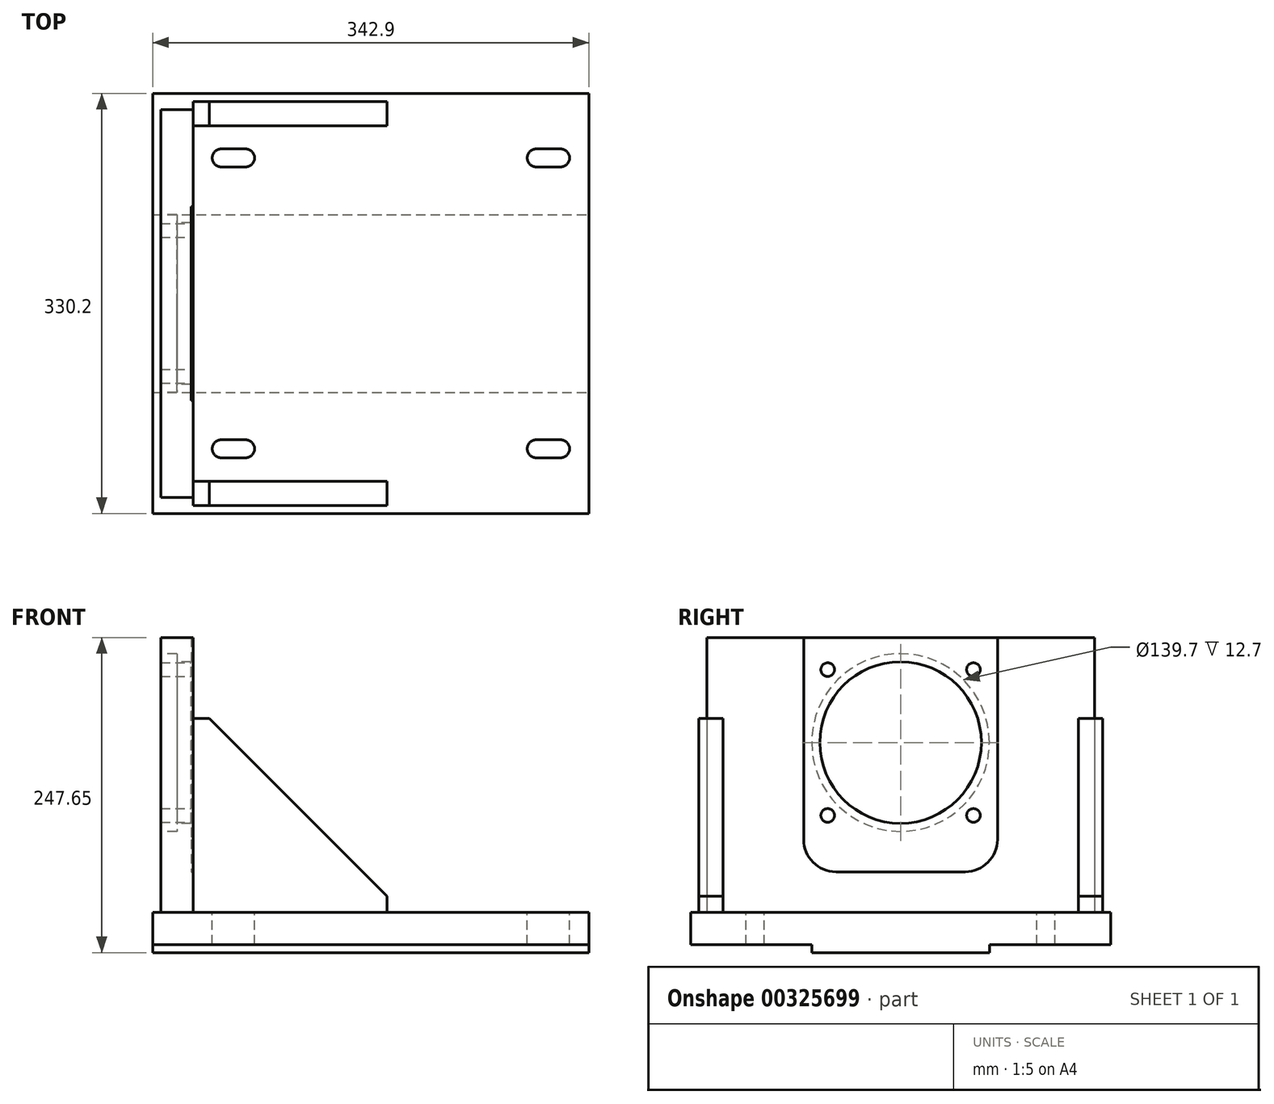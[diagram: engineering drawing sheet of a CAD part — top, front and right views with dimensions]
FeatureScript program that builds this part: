
annotation { "Feature Type Name" : "Feature", "Feature Type Description" : "" }
export const myFeature = defineFeature(function(context is Context, id is Id, definition is map)
    precondition{}
    {
        {
            var Q0;
            Q0=qCreatedBy(makeId("Top.planeOp"),FACE);
            var sketch = newSketch(context, id + "F0", { "sketchPlane" : qUnion([Q0])});
            skLineSegment(sketch, "E0.bottom", {"start": v(-171.45, 165.1) * mm, "end": v(171.45, 165.1) * mm});
            skLineSegment(sketch, "E0.top", {"start": v(-171.45, -165.1) * mm, "end": v(171.45, -165.1) * mm});
            skLineSegment(sketch, "E0.left", {"start": v(-171.45, 165.1) * mm, "end": v(-171.45, -165.1) * mm});
            skLineSegment(sketch, "E0.right", {"start": v(171.45, 165.1) * mm, "end": v(171.45, -165.1) * mm});
            skPoint(sketch, "E0.middle", {"position": v(0, 0) * mm});
            skLineSegment(sketch, "E1.0", {"start": v(149.23, 165.1) * mm, "end": v(149.22, -165.1) * mm, "construction": true});
            skLineSegment(sketch, "E2.0", {"start": v(130.18, 165.1) * mm, "end": v(130.17, -165.1) * mm, "construction": true});
            skLineSegment(sketch, "E3", {"start": v(-287.48, 0) * mm, "end": v(272.76, 0) * mm, "construction": true});
            skPoint(sketch, "E3.endSnap0", {"position": v(171.45, 0) * mm});
            skLineSegment(sketch, "E4.0", {"start": v(-287.48, -114.3) * mm, "end": v(-171.45, -114.3) * mm, "construction": true});
            skLineSegment(sketch, "E5.0", {"start": v(-98.42, 165.1) * mm, "end": v(-98.43, -165.1) * mm, "construction": true});
            skLineSegment(sketch, "E6.0", {"start": v(-117.47, 165.1) * mm, "end": v(-117.48, -165.1) * mm, "construction": true});
            skLineSegment(sketch, "E7.trimOffspring", {"start": v(-117.48, -114.3) * mm, "end": v(-98.43, -114.3) * mm});
            skLineSegment(sketch, "E8.trimOffspring", {"start": v(130.17, -114.3) * mm, "end": v(149.22, -114.3) * mm});
            skLineSegment(sketch, "E9.trimOffspring", {"start": v(171.45, -114.3) * mm, "end": v(272.76, -114.3) * mm, "construction": true});
            skArc(sketch, "E10.0.startCap", {"start": v(-117.48, -121.41) * mm, "mid": v(-124.59, -114.3) * mm, "end": v(-117.48, -107.19) * mm});
            skArc(sketch, "E10.0.endCap", {"start": v(-98.43, -107.19) * mm, "mid": v(-91.31, -114.3) * mm, "end": v(-98.43, -121.41) * mm});
            skLineSegment(sketch, "E10.0.left", {"start": v(-117.48, -107.19) * mm, "end": v(-98.43, -107.19) * mm});
            skLineSegment(sketch, "E10.0.right", {"start": v(-117.48, -121.41) * mm, "end": v(-98.43, -121.41) * mm});
            skArc(sketch, "E10.1.startCap", {"start": v(130.17, -121.41) * mm, "mid": v(123.06, -114.3) * mm, "end": v(130.17, -107.19) * mm});
            skArc(sketch, "E10.1.endCap", {"start": v(149.22, -107.19) * mm, "mid": v(156.34, -114.3) * mm, "end": v(149.22, -121.41) * mm});
            skLineSegment(sketch, "E10.1.left", {"start": v(130.17, -107.19) * mm, "end": v(149.22, -107.19) * mm});
            skLineSegment(sketch, "E10.1.right", {"start": v(130.17, -121.41) * mm, "end": v(149.22, -121.41) * mm});
            skLineSegment(sketch, "E11.MirrorCS", {"start": v(-117.48, 114.3) * mm, "end": v(-98.43, 114.3) * mm});
            skLineSegment(sketch, "E12.MirrorCS", {"start": v(-117.48, 107.19) * mm, "end": v(-98.43, 107.19) * mm});
            skLineSegment(sketch, "E13.MirrorCS", {"start": v(130.17, 107.19) * mm, "end": v(149.22, 107.19) * mm});
            skLineSegment(sketch, "E14.MirrorCS", {"start": v(130.17, 114.3) * mm, "end": v(149.22, 114.3) * mm});
            skLineSegment(sketch, "E15.MirrorCS", {"start": v(130.17, 121.41) * mm, "end": v(149.22, 121.41) * mm});
            skArc(sketch, "E16.MirrorCS", {"start": v(-117.48, 121.41) * mm, "mid": v(-124.59, 114.3) * mm, "end": v(-117.48, 107.19) * mm});
            skArc(sketch, "E17.MirrorCS", {"start": v(130.18, 121.41) * mm, "mid": v(123.06, 114.3) * mm, "end": v(130.18, 107.19) * mm});
            skLineSegment(sketch, "E18.MirrorCS", {"start": v(-117.48, 121.41) * mm, "end": v(-98.43, 121.41) * mm});
            skArc(sketch, "E19.MirrorCS", {"start": v(-98.43, 107.19) * mm, "mid": v(-91.31, 114.3) * mm, "end": v(-98.43, 121.41) * mm});
            skArc(sketch, "E20.MirrorCS", {"start": v(149.23, 107.19) * mm, "mid": v(156.34, 114.3) * mm, "end": v(149.23, 121.41) * mm});
            skSolve(sketch);
        }
        {
            var Q0;
            Q0=qSketchRegion(id+"F0",true);
            extrude(context, id + "F1", {"entities" : qUnion([Q0]), "oppositeDirection" : true, "depth" : 25.4 * mm});
        }
        {
            var Q0;
            Q0=makeQuery(id+"F1.opExtrude","CAP_FACE",FACE,{"disambiguationData":[OSD([sQuery(id+"F0.wireOp",EDGE,"E0.bottom"),sQuery(id+"F0.wireOp",EDGE,"E0.top"),sQuery(id+"F0.wireOp",EDGE,"E0.left"),sQuery(id+"F0.wireOp",EDGE,"E0.right"),sQuery(id+"F0.wireOp",EDGE,"E10.0.startCap"),sQuery(id+"F0.wireOp",EDGE,"E10.0.endCap"),sQuery(id+"F0.wireOp",EDGE,"E10.0.left"),sQuery(id+"F0.wireOp",EDGE,"E10.0.right"),sQuery(id+"F0.wireOp",EDGE,"E10.1.startCap"),sQuery(id+"F0.wireOp",EDGE,"E10.1.endCap"),sQuery(id+"F0.wireOp",EDGE,"E10.1.left"),sQuery(id+"F0.wireOp",EDGE,"E10.1.right"),sQuery(id+"F0.wireOp",EDGE,"E12.MirrorCS"),sQuery(id+"F0.wireOp",EDGE,"E13.MirrorCS"),sQuery(id+"F0.wireOp",EDGE,"E15.MirrorCS"),sQuery(id+"F0.wireOp",EDGE,"E16.MirrorCS"),sQuery(id+"F0.wireOp",EDGE,"E17.MirrorCS"),sQuery(id+"F0.wireOp",EDGE,"E18.MirrorCS"),sQuery(id+"F0.wireOp",EDGE,"E19.MirrorCS"),sQuery(id+"F0.wireOp",EDGE,"E20.MirrorCS")])],"isStart":false});
            var sketch = newSketch(context, id + "F2", { "sketchPlane" : qUnion([Q0])});
            skLineSegment(sketch, "E21.bottom", {"start": v(-171.45, 69.85) * mm, "end": v(171.45, 69.85) * mm});
            skLineSegment(sketch, "E21.top", {"start": v(-171.45, -69.85) * mm, "end": v(171.45, -69.85) * mm});
            skLineSegment(sketch, "E21.left", {"start": v(-171.45, 69.85) * mm, "end": v(-171.45, -69.85) * mm});
            skLineSegment(sketch, "E21.right", {"start": v(171.45, 69.85) * mm, "end": v(171.45, -69.85) * mm});
            skPoint(sketch, "E21.middle", {"position": v(0, 0) * mm});
            skSolve(sketch);
        }
        {
            var Q0;
            Q0=qSketchRegion(id+"F2",true);
            extrude(context, id + "F3", {"entities" : qUnion([Q0]), "operationType" : NewBodyOperationType.ADD, "depth" : 6.35 * mm});
        }
        {
            var Q0;
            Q0=makeQuery(id+"F1.opExtrude","CAP_FACE",FACE,{"disambiguationData":[OSD([sQuery(id+"F0.wireOp",EDGE,"E0.bottom"),sQuery(id+"F0.wireOp",EDGE,"E0.top"),sQuery(id+"F0.wireOp",EDGE,"E0.left"),sQuery(id+"F0.wireOp",EDGE,"E0.right"),sQuery(id+"F0.wireOp",EDGE,"E10.0.startCap"),sQuery(id+"F0.wireOp",EDGE,"E10.0.endCap"),sQuery(id+"F0.wireOp",EDGE,"E10.0.left"),sQuery(id+"F0.wireOp",EDGE,"E10.0.right"),sQuery(id+"F0.wireOp",EDGE,"E10.1.startCap"),sQuery(id+"F0.wireOp",EDGE,"E10.1.endCap"),sQuery(id+"F0.wireOp",EDGE,"E10.1.left"),sQuery(id+"F0.wireOp",EDGE,"E10.1.right"),sQuery(id+"F0.wireOp",EDGE,"E12.MirrorCS"),sQuery(id+"F0.wireOp",EDGE,"E13.MirrorCS"),sQuery(id+"F0.wireOp",EDGE,"E15.MirrorCS"),sQuery(id+"F0.wireOp",EDGE,"E16.MirrorCS"),sQuery(id+"F0.wireOp",EDGE,"E17.MirrorCS"),sQuery(id+"F0.wireOp",EDGE,"E18.MirrorCS"),sQuery(id+"F0.wireOp",EDGE,"E19.MirrorCS"),sQuery(id+"F0.wireOp",EDGE,"E20.MirrorCS")])],"isStart":true});
            var sketch = newSketch(context, id + "F4", { "sketchPlane" : qUnion([Q0])});
            skLineSegment(sketch, "E22.0", {"start": v(-165.1, 152.4) * mm, "end": v(-165.1, -152.4) * mm});
            skLineSegment(sketch, "E23.0", {"start": v(-139.7, 152.4) * mm, "end": v(-139.7, -152.4) * mm});
            skLineSegment(sketch, "E24", {"start": v(-299.95, 0) * mm, "end": v(210.66, 0) * mm, "construction": true});
            skLineSegment(sketch, "E25.0", {"start": v(-165.1, -152.4) * mm, "end": v(-139.7, -152.4) * mm});
            skLineSegment(sketch, "E26.MirrorCS", {"start": v(-165.1, 152.4) * mm, "end": v(-139.7, 152.4) * mm});
            skSolve(sketch);
        }
        {
            var Q0;
            Q0=qSketchRegion(id+"F4",true);
            extrude(context, id + "F5", {"entities" : qUnion([Q0]), "operationType" : NewBodyOperationType.ADD, "depth" : 215.9 * mm});
        }
        {
            var Q0;
            Q0=makeQuery(id+"F5.opExtrude","SWEPT_FACE",FACE,{"disambiguationData":[OSD([sQuery(id+"F4.wireOp",EDGE,"E22.0")])]});
            var sketch = newSketch(context, id + "F6", { "sketchPlane" : qUnion([Q0])});
            skLineSegment(sketch, "E27.0", {"start": v(-152.4, 133.35) * mm, "end": v(152.4, 133.35) * mm, "construction": true});
            skPoint(sketch, "E28", {"position": v(0, 133.35) * mm});
            skSolve(sketch);
        }
        {
            var Q0;
            Q0=sQuery(id+"F6.wireOp",VERTEX,"E28");
            var Q1;
            Q1=makeQuery(id+"F1.opExtrude","SWEPT_BODY",BODY,{"disambiguationData":[OSD([sQuery(id+"F0.wireOp",EDGE,"E0.bottom"),sQuery(id+"F0.wireOp",EDGE,"E0.top"),sQuery(id+"F0.wireOp",EDGE,"E0.left"),sQuery(id+"F0.wireOp",EDGE,"E0.right"),sQuery(id+"F0.wireOp",EDGE,"E10.0.startCap"),sQuery(id+"F0.wireOp",EDGE,"E10.0.endCap"),sQuery(id+"F0.wireOp",EDGE,"E10.0.left"),sQuery(id+"F0.wireOp",EDGE,"E10.0.right"),sQuery(id+"F0.wireOp",EDGE,"E10.1.startCap"),sQuery(id+"F0.wireOp",EDGE,"E10.1.endCap"),sQuery(id+"F0.wireOp",EDGE,"E10.1.left"),sQuery(id+"F0.wireOp",EDGE,"E10.1.right"),sQuery(id+"F0.wireOp",EDGE,"E12.MirrorCS"),sQuery(id+"F0.wireOp",EDGE,"E13.MirrorCS"),sQuery(id+"F0.wireOp",EDGE,"E15.MirrorCS"),sQuery(id+"F0.wireOp",EDGE,"E16.MirrorCS"),sQuery(id+"F0.wireOp",EDGE,"E17.MirrorCS"),sQuery(id+"F0.wireOp",EDGE,"E18.MirrorCS"),sQuery(id+"F0.wireOp",EDGE,"E19.MirrorCS"),sQuery(id+"F0.wireOp",EDGE,"E20.MirrorCS")])]});
            hole(context, id + "F7", {"style" : HoleStyle.C_BORE, "endStyle" : HoleEndStyle.THROUGH, "holeDiameter" : 127 * mm, "cBoreDiameter" : 139.7 * mm, "cBoreDepth" : 12.7 * mm, "tappedDepth" : 10 * mm, "tapClearance" : 3, "locations" : qUnion([Q0]), "scope" : qUnion([Q1])});
        }
        {
            var Q0;
            Q0=makeQuery(id+"F5.opExtrude","SWEPT_FACE",FACE,{"disambiguationData":[OSD([sQuery(id+"F4.wireOp",EDGE,"E23.0")])]});
            var sketch = newSketch(context, id + "F8", { "sketchPlane" : qUnion([Q0])});
            skCircle(sketch, "E29.0", {"center": v(0, 133.35) * mm, "radius": 63.5 * mm, "construction": true});
            skLineSegment(sketch, "E30.0", {"start": v(50.8, 31.75) * mm, "end": v(-50.8, 31.75) * mm});
            skLineSegment(sketch, "E31", {"start": v(0, 360.03) * mm, "end": v(0, -161.05) * mm});
            skLineSegment(sketch, "E32.0", {"start": v(-76.2, 360.03) * mm, "end": v(-76.2, 57.15) * mm});
            skLineSegment(sketch, "E33.0", {"start": v(152.4, 215.9) * mm, "end": v(-152.4, 215.9) * mm});
            skLineSegment(sketch, "E34.MirrorCS", {"start": v(76.2, 360.03) * mm, "end": v(76.2, 57.15) * mm});
            skPoint(sketch, "E35.newPointA", {"position": v(76.2, -161.05) * mm});
            skArc(sketch, "E35.filletArc", {"start": v(50.8, 31.75) * mm, "mid": v(68.76, 39.19) * mm, "end": v(76.2, 57.15) * mm});
            skPoint(sketch, "E36.newPointB", {"position": v(-76.2, -161.05) * mm});
            skArc(sketch, "E36.filletArc", {"start": v(-76.2, 57.15) * mm, "mid": v(-68.76, 39.19) * mm, "end": v(-50.8, 31.75) * mm});
            skSolve(sketch);
        }
        {
            var Q0;
            Q0=qSketchRegion(id+"F8",true);
            extrude(context, id + "F9", {"entities" : qUnion([Q0]), "operationType" : NewBodyOperationType.REMOVE, "oppositeDirection" : true, "depth" : 1.52 * mm});
        }
        {
            var Q0;
            Q0=makeQuery(id+"F9.boolean.opBoolean","COPY",FACE,{"derivedFrom":makeQuery(id+"F9.opExtrude","CAP_FACE",FACE,{"disambiguationData":[OSD([sQuery(id+"F8.wireOp",EDGE,"E30.0"),sQuery(id+"F8.wireOp",EDGE,"E32.0"),sQuery(id+"F8.wireOp",EDGE,"E33.0"),sQuery(id+"F8.wireOp",EDGE,"E34.MirrorCS"),sQuery(id+"F8.wireOp",EDGE,"E35.filletArc"),sQuery(id+"F8.wireOp",EDGE,"E36.filletArc")])],"isStart":false})});
            var sketch = newSketch(context, id + "F10", { "sketchPlane" : qUnion([Q0])});
            skCircle(sketch, "E37.0", {"center": v(0, 133.35) * mm, "radius": 63.5 * mm, "construction": true});
            skCircle(sketch, "E38", {"center": v(0, 133.35) * mm, "radius": 81.03 * mm, "construction": true});
            skLineSegment(sketch, "E39", {"start": v(0, 133.35) * mm, "end": v(0, 285.7) * mm, "construction": true});
            skLineSegment(sketch, "E40", {"start": v(0, 133.35) * mm, "end": v(155.7, 289.05) * mm, "construction": true});
            skPoint(sketch, "E41", {"position": v(57.3, 190.64) * mm});
            skPoint(sketch, "E42.1.0", {"position": v(-57.3, 190.64) * mm});
            skPoint(sketch, "E42.2.0", {"position": v(-57.3, 76.06) * mm});
            skPoint(sketch, "E42.3.0", {"position": v(57.3, 76.06) * mm});
            skSolve(sketch);
        }
        {
            var Q0;
            Q0=sQuery(id+"F10.wireOp",VERTEX,"E41");
            var Q1;
            Q1=sQuery(id+"F10.wireOp",VERTEX,"E42.3.0");
            var Q2;
            Q2=sQuery(id+"F10.wireOp",VERTEX,"E42.2.0");
            var Q3;
            Q3=sQuery(id+"F10.wireOp",VERTEX,"E42.1.0");
            var Q4;
            Q4=makeQuery(id+"F1.opExtrude","SWEPT_BODY",BODY,{"disambiguationData":[OSD([sQuery(id+"F0.wireOp",EDGE,"E0.bottom"),sQuery(id+"F0.wireOp",EDGE,"E0.top"),sQuery(id+"F0.wireOp",EDGE,"E0.left"),sQuery(id+"F0.wireOp",EDGE,"E0.right"),sQuery(id+"F0.wireOp",EDGE,"E10.0.startCap"),sQuery(id+"F0.wireOp",EDGE,"E10.0.endCap"),sQuery(id+"F0.wireOp",EDGE,"E10.0.left"),sQuery(id+"F0.wireOp",EDGE,"E10.0.right"),sQuery(id+"F0.wireOp",EDGE,"E10.1.startCap"),sQuery(id+"F0.wireOp",EDGE,"E10.1.endCap"),sQuery(id+"F0.wireOp",EDGE,"E10.1.left"),sQuery(id+"F0.wireOp",EDGE,"E10.1.right"),sQuery(id+"F0.wireOp",EDGE,"E12.MirrorCS"),sQuery(id+"F0.wireOp",EDGE,"E13.MirrorCS"),sQuery(id+"F0.wireOp",EDGE,"E15.MirrorCS"),sQuery(id+"F0.wireOp",EDGE,"E16.MirrorCS"),sQuery(id+"F0.wireOp",EDGE,"E17.MirrorCS"),sQuery(id+"F0.wireOp",EDGE,"E18.MirrorCS"),sQuery(id+"F0.wireOp",EDGE,"E19.MirrorCS"),sQuery(id+"F0.wireOp",EDGE,"E20.MirrorCS")])]});
            hole(context, id + "F11", {"style" : HoleStyle.SIMPLE, "endStyle" : HoleEndStyle.THROUGH, "standardTappedOrClearance" : lookupTablePath({ "standard" : "ANSI", "engagement" : "75%", "pitch" : "13 tpi", "size" : "1/2", "type" : "Tapped" }), "standardBlindInLast" : lookupTablePath({ "standard" : "ANSI", "engagement" : "75%", "pitch" : "13 tpi", "size" : "1/2", "type" : "Tapped" }), "holeDiameter" : 10.72 * mm, "showTappedDepth" : true, "tappedDepth" : 10 * mm, "tapClearance" : 3, "locations" : qUnion([Q0, Q1, Q2, Q3]), "scope" : qUnion([Q4]), "majorDiameter" : 12.7 * mm});
        }
        {
            var Q0;
            Q0=makeQuery(id+"F1.opExtrude","CAP_FACE",FACE,{"disambiguationData":[OSD([sQuery(id+"F0.wireOp",EDGE,"E0.bottom"),sQuery(id+"F0.wireOp",EDGE,"E0.top"),sQuery(id+"F0.wireOp",EDGE,"E0.left"),sQuery(id+"F0.wireOp",EDGE,"E0.right"),sQuery(id+"F0.wireOp",EDGE,"E10.0.startCap"),sQuery(id+"F0.wireOp",EDGE,"E10.0.endCap"),sQuery(id+"F0.wireOp",EDGE,"E10.0.left"),sQuery(id+"F0.wireOp",EDGE,"E10.0.right"),sQuery(id+"F0.wireOp",EDGE,"E10.1.startCap"),sQuery(id+"F0.wireOp",EDGE,"E10.1.endCap"),sQuery(id+"F0.wireOp",EDGE,"E10.1.left"),sQuery(id+"F0.wireOp",EDGE,"E10.1.right"),sQuery(id+"F0.wireOp",EDGE,"E12.MirrorCS"),sQuery(id+"F0.wireOp",EDGE,"E13.MirrorCS"),sQuery(id+"F0.wireOp",EDGE,"E15.MirrorCS"),sQuery(id+"F0.wireOp",EDGE,"E16.MirrorCS"),sQuery(id+"F0.wireOp",EDGE,"E17.MirrorCS"),sQuery(id+"F0.wireOp",EDGE,"E18.MirrorCS"),sQuery(id+"F0.wireOp",EDGE,"E19.MirrorCS"),sQuery(id+"F0.wireOp",EDGE,"E20.MirrorCS")])],"isStart":true});
            var sketch = newSketch(context, id + "F12", { "sketchPlane" : qUnion([Q0])});
            skLineSegment(sketch, "E43.0", {"start": v(-139.7, 158.75) * mm, "end": v(12.7, 158.75) * mm});
            skLineSegment(sketch, "E44.0", {"start": v(12.7, 158.75) * mm, "end": v(12.7, 139.7) * mm});
            skLineSegment(sketch, "E45.0", {"start": v(-139.7, 139.7) * mm, "end": v(12.7, 139.7) * mm});
            skPoint(sketch, "E46.0", {"position": v(-139.7, 114.3) * mm});
            skLineSegment(sketch, "E47.0", {"start": v(-139.7, 158.75) * mm, "end": v(-139.7, 139.7) * mm});
            skPoint(sketch, "E48.orphan", {"position": v(-139.7, 152.4) * mm});
            skPoint(sketch, "E49.orphan", {"position": v(-139.7, 76.2) * mm});
            skLineSegment(sketch, "E50", {"start": v(-224.57, 0) * mm, "end": v(197.35, 0) * mm, "construction": true});
            skLineSegment(sketch, "E51.MirrorCS", {"start": v(-139.7, -158.75) * mm, "end": v(-139.7, -139.7) * mm});
            skPoint(sketch, "E52.MirrorP", {"position": v(-139.7, -152.4) * mm});
            skLineSegment(sketch, "E53.MirrorCS", {"start": v(-139.7, -158.75) * mm, "end": v(12.7, -158.75) * mm});
            skPoint(sketch, "E54.MirrorP", {"position": v(-139.7, -114.3) * mm});
            skLineSegment(sketch, "E55.MirrorCS", {"start": v(12.7, -158.75) * mm, "end": v(12.7, -139.7) * mm});
            skLineSegment(sketch, "E56.MirrorCS", {"start": v(-139.7, -139.7) * mm, "end": v(12.7, -139.7) * mm});
            skSolve(sketch);
        }
        {
            var Q0;
            Q0=qSketchRegion(id+"F12",true);
            extrude(context, id + "F13", {"entities" : qUnion([Q0]), "operationType" : NewBodyOperationType.ADD, "depth" : 152.4 * mm});
        }
        {
            var Q0;
            Q0=makeQuery(id+"F13.opExtrude","CAP_EDGE",EDGE,{"disambiguationData":[OSD([sQuery(id+"F12.wireOp",EDGE,"E44.0")])],"isStart":false});
            var Q1;
            Q1=makeQuery(id+"F13.opExtrude","CAP_EDGE",EDGE,{"disambiguationData":[OSD([sQuery(id+"F12.wireOp",EDGE,"E55.MirrorCS")])],"isStart":false});
            chamfer(context, id + "F14", {"entities" : qUnion([Q0, Q1]), "width" : 139.7 * mm, "tangentPropagation" : true});
        }
    });
